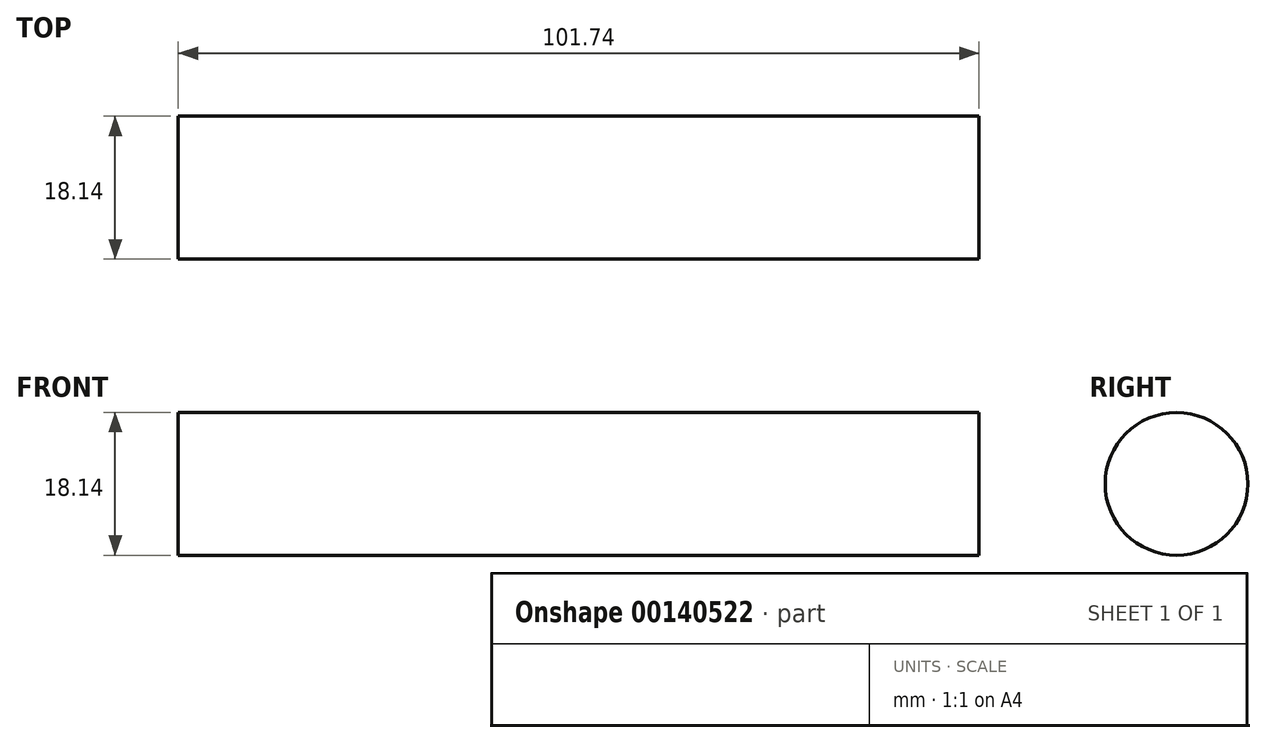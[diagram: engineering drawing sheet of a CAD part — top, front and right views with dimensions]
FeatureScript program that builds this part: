
annotation { "Feature Type Name" : "Feature", "Feature Type Description" : "" }
export const myFeature = defineFeature(function(context is Context, id is Id, definition is map)
    precondition{}
    {
        {
            var Q0;
            Q0=qCreatedBy(makeId("Right.planeOp"),FACE);
            var sketch = newSketch(context, id + "F0", { "sketchPlane" : qUnion([Q0])});
            skCircle(sketch, "E0", {"center": v(0, 0) * mm, "radius": 9.07 * mm});
            skSolve(sketch);
        }
        {
            var Q0;
            Q0=makeQuery(id+"F0.imprint","IMPRINT",FACE,{"disambiguationData":[TD([[makeQuery(id+"F0.imprint","IMPRINT",EDGE,{"derivedFrom":sQuery(id+"F0.wireOp",EDGE,"E0")}),1.0]])]});
            extrude(context, id + "F1", {"entities" : qUnion([Q0]), "depth" : 101.74 * mm});
        }
    });
